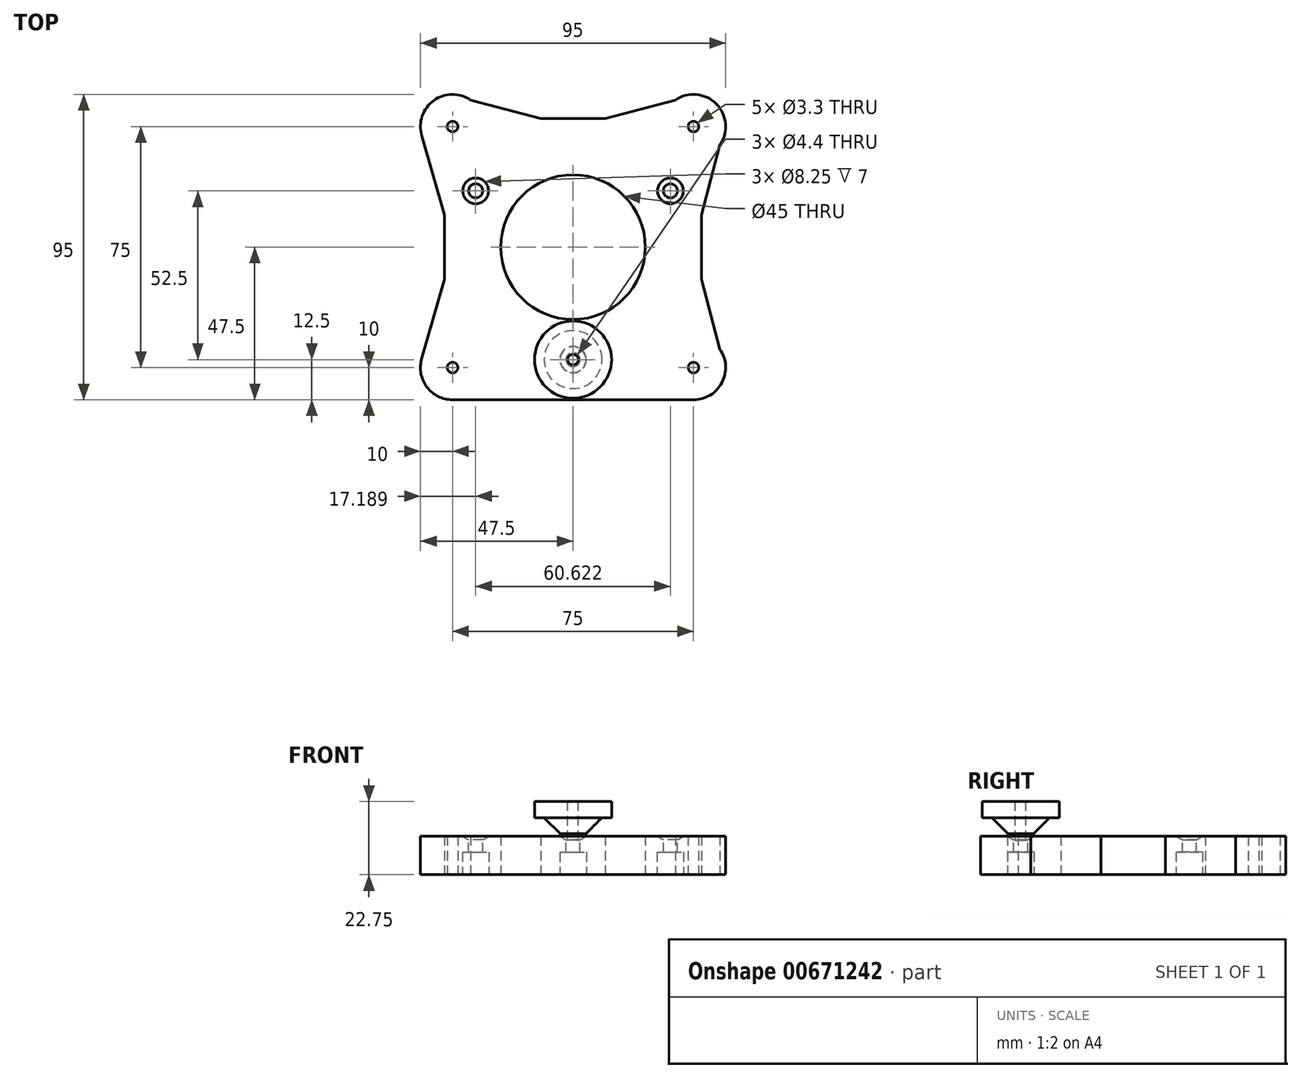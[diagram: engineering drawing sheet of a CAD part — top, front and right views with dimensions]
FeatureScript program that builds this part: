
annotation { "Feature Type Name" : "Feature", "Feature Type Description" : "" }
export const myFeature = defineFeature(function(context is Context, id is Id, definition is map)
    precondition{}
    {
        {
            var Q0;
            Q0=qCreatedBy(makeId("Top.planeOp"),FACE);
            var sketch = newSketch(context, id + "F0", { "sketchPlane" : qUnion([Q0])});
            skLineSegment(sketch, "E0", {"start": v(0, -66.49) * mm, "end": v(0, 82.54) * mm, "construction": true});
            skLineSegment(sketch, "E1", {"start": v(68.94, 0) * mm, "end": v(-65.72, 0) * mm, "construction": true});
            skLineSegment(sketch, "E2.MirrorCS", {"start": v(-68.94, 0) * mm, "end": v(65.72, 0) * mm, "construction": true});
            skArc(sketch, "E3", {"start": v(-31.85, 45.75) * mm, "mid": v(-43.35, 45.6) * mm, "end": v(-47.11, 34.74) * mm});
            skArc(sketch, "E4", {"start": v(45.75, 31.85) * mm, "mid": v(44.57, 44.57) * mm, "end": v(31.85, 45.75) * mm});
            skArc(sketch, "E5", {"start": v(37.5, -47.5) * mm, "mid": v(46.35, -42.16) * mm, "end": v(45.75, -31.85) * mm});
            skArc(sketch, "E6", {"start": v(-47.11, -34.74) * mm, "mid": v(-45.49, -43.52) * mm, "end": v(-37.5, -47.5) * mm});
            skLineSegment(sketch, "E7", {"start": v(-40, -10) * mm, "end": v(-40, 10) * mm});
            skLineSegment(sketch, "E8", {"start": v(-40, 10) * mm, "end": v(-47.11, 34.74) * mm});
            skLineSegment(sketch, "E9", {"start": v(-40, -10) * mm, "end": v(-47.11, -34.74) * mm});
            skLineSegment(sketch, "E10.2.0", {"start": v(40, 10) * mm, "end": v(40, -10) * mm});
            skLineSegment(sketch, "E10.2.1", {"start": v(40, -10) * mm, "end": v(45.75, -31.85) * mm});
            skLineSegment(sketch, "E10.2.2", {"start": v(40, 10) * mm, "end": v(45.75, 31.85) * mm});
            skLineSegment(sketch, "E10.3.0", {"start": v(-10, 40) * mm, "end": v(10, 40) * mm});
            skLineSegment(sketch, "E10.3.1", {"start": v(10, 40) * mm, "end": v(31.85, 45.75) * mm});
            skLineSegment(sketch, "E10.3.2", {"start": v(-10, 40) * mm, "end": v(-31.85, 45.75) * mm});
            skPoint(sketch, "E10.center", {"position": v(0, 0) * mm});
            skLineSegment(sketch, "E11", {"start": v(-37.5, -47.5) * mm, "end": v(37.5, -47.5) * mm});
            skSolve(sketch);
        }
        {
            var Q0;
            Q0=makeQuery(id+"F0.imprint","IMPRINT",FACE,{"disambiguationData":[TD([[makeQuery(id+"F0.imprint","IMPRINT",EDGE,{"derivedFrom":sQuery(id+"F0.wireOp",EDGE,"E3")}),1.0]])]});
            extrude(context, id + "F1", {"entities" : qUnion([Q0]), "depth" : 12 * mm, "offsetDistance" : 25 * mm});
        }
        {
            var Q0;
            Q0=makeQuery(id+"F1.opExtrude","CAP_FACE",FACE,{"disambiguationData":[OSD([sQuery(id+"F0.wireOp",EDGE,"H59K7WDl-hRpV-Jpdm-ny2t-aA3Kgsrr1DyG"),sQuery(id+"F0.wireOp",EDGE,"7fe8aba1-2dff-4e51-9fbd-37248f7f35f50.MirrorC"),sQuery(id+"F0.wireOp",EDGE,"c00ab9d0-4618-4e23-ab7e-bcd3a19236070.MirrorC"),sQuery(id+"F0.wireOp",EDGE,"2b578c46-e155-4f13-8c82-5516d9e6c2640.MirrorC"),sQuery(id+"F0.wireOp",EDGE,"E3"),sQuery(id+"F0.wireOp",EDGE,"E4"),sQuery(id+"F0.wireOp",EDGE,"E5"),sQuery(id+"F0.wireOp",EDGE,"E6"),sQuery(id+"F0.wireOp",EDGE,"E7"),sQuery(id+"F0.wireOp",EDGE,"E8"),sQuery(id+"F0.wireOp",EDGE,"E9"),sQuery(id+"F0.wireOp",EDGE,"E10.1.1"),sQuery(id+"F0.wireOp",EDGE,"E10.1.2"),sQuery(id+"F0.wireOp",EDGE,"E10.2.0"),sQuery(id+"F0.wireOp",EDGE,"E10.2.1"),sQuery(id+"F0.wireOp",EDGE,"E10.2.2"),sQuery(id+"F0.wireOp",EDGE,"E10.3.0"),sQuery(id+"F0.wireOp",EDGE,"E10.3.1"),sQuery(id+"F0.wireOp",EDGE,"E10.3.2"),sQuery(id+"F0.wireOp",EDGE,"E11")])],"isStart":false});
            var sketch = newSketch(context, id + "F2", { "sketchPlane" : qUnion([Q0])});
            skLineSegment(sketch, "E12", {"start": v(0, 0) * mm, "end": v(0, -80.34) * mm, "construction": true});
            skPoint(sketch, "E13", {"position": v(0, -35) * mm});
            skPoint(sketch, "E14.center", {"position": v(0, 0) * mm});
            skPoint(sketch, "E15.1.0", {"position": v(30.31, 17.5) * mm});
            skPoint(sketch, "E15.2.0", {"position": v(-30.31, 17.5) * mm});
            skLineSegment(sketch, "E16", {"start": v(0, -20.19) * mm, "end": v(0, -35) * mm, "construction": true});
            skLineSegment(sketch, "E17.1.0", {"start": v(17.48, 10.1) * mm, "end": v(30.31, 17.5) * mm, "construction": true});
            skLineSegment(sketch, "E17.2.0", {"start": v(-17.48, 10.1) * mm, "end": v(-30.31, 17.5) * mm, "construction": true});
            skSolve(sketch);
        }
        {
            var Q0;
            Q0=sQuery(id+"F2.wireOp",VERTEX,"E13");
            var Q1;
            Q1=makeQuery(id+"F1.opExtrude","SWEPT_FACE",FACE,{"disambiguationData":[OSD([sQuery(id+"F0.wireOp",EDGE,"E10.3.0")])]});
            cPlane(context, id + "F3", {"entities" : qUnion([Q0, Q1]), "cplaneType" : CPlaneType.PLANE_POINT, "offset" : 25 * mm, "width" : 150 * mm, "height" : 150 * mm});
        }
        {
            var Q0;
            Q0=qCreatedBy(id+"F3.planeOp",FACE);
            var sketch = newSketch(context, id + "F4", { "sketchPlane" : qUnion([Q0])});
            skLineSegment(sketch, "E18", {"start": v(4, 12) * mm, "end": v(0, 12) * mm});
            skArc(sketch, "E19", {"start": v(0, 10.47) * mm, "mid": v(2.14, 10.87) * mm, "end": v(4, 12) * mm});
            skLineSegment(sketch, "E20", {"start": v(0, 12) * mm, "end": v(0, 40.48) * mm, "construction": true});
            skLineSegment(sketch, "E21", {"start": v(0, 12) * mm, "end": v(0, 10.47) * mm});
            skLineSegment(sketch, "E22.trimOffspring", {"start": v(0, 12) * mm, "end": v(4, 12) * mm});
            skPoint(sketch, "E23.0.8.end.orphan", {"position": v(-4, 12) * mm});
            skPoint(sketch, "E23.0.8.start.orphan", {"position": v(-10, 12) * mm});
            skPoint(sketch, "E24.orphan", {"position": v(10, 12) * mm});
            skSolve(sketch);
        }
        {
            var Q0;
            Q0=sQuery(id+"F2.wireOp",EDGE,"E17.2.0");
            cPlane(context, id + "F5", {"entities" : qUnion([Q0]), "cplaneType" : CPlaneType.LINE_ANGLE, "offset" : 25 * mm, "angle" : 0 * degree, "width" : 150 * mm, "height" : 150 * mm});
        }
        {
            var Q0;
            Q0=qCreatedBy(id+"F5.planeOp",FACE);
            var sketch = newSketch(context, id + "F6", { "sketchPlane" : qUnion([Q0])});
            skLineSegment(sketch, "E25", {"start": v(-31, 12) * mm, "end": v(-35, 12) * mm});
            skArc(sketch, "E26", {"start": v(-35, 10.47) * mm, "mid": v(-32.86, 10.87) * mm, "end": v(-31, 12) * mm});
            skLineSegment(sketch, "E27", {"start": v(-35, 12) * mm, "end": v(-35, 40.48) * mm, "construction": true});
            skLineSegment(sketch, "E28", {"start": v(-35, 12) * mm, "end": v(-35, 10.47) * mm});
            skLineSegment(sketch, "E29.trimOffspring", {"start": v(-35, 12) * mm, "end": v(-31, 12) * mm});
            skPoint(sketch, "E30.0.8.end.orphan", {"position": v(-39, 12) * mm});
            skPoint(sketch, "E30.0.8.start.orphan", {"position": v(-45, 12) * mm});
            skPoint(sketch, "E31.orphan", {"position": v(-25, 12) * mm});
            skSolve(sketch);
        }
        {
            var Q0;
            {var subQ0=sQuery(id+"F4.wireOp",EDGE,"E19");Q0=makeQuery(id+"F4.imprint","IMPRINT",FACE,{"disambiguationData":[TD([[makeQuery(id+"F4.imprint","IMPRINT",EDGE,{"derivedFrom":subQ0}),1.0]])]});}
            var Q1;
            Q1=sQuery(id+"F4.wireOp",EDGE,"E20");
            revolve(context, id + "F7", {"operationType" : NewBodyOperationType.REMOVE, "entities" : qUnion([Q0]), "axis" : qUnion([Q1]), "revolveType" : RevolveType.FULL, "oppositeDirection" : true});
        }
        {
            var Q0;
            Q0=makeQuery(id+"F6.imprint","IMPRINT",FACE,{"disambiguationData":[TD([[makeQuery(id+"F6.imprint","IMPRINT",EDGE,{"derivedFrom":sQuery(id+"F6.wireOp",EDGE,"E26")}),1.0]])]});
            var Q1;
            Q1=sQuery(id+"F6.wireOp",EDGE,"E27");
            revolve(context, id + "F8", {"operationType" : NewBodyOperationType.REMOVE, "entities" : qUnion([Q0]), "axis" : qUnion([Q1]), "revolveType" : RevolveType.FULL, "oppositeDirection" : true});
        }
        {
            var Q0;
            Q0=sQuery(id+"F2.wireOp",EDGE,"E17.1.0");
            cPlane(context, id + "F9", {"entities" : qUnion([Q0]), "cplaneType" : CPlaneType.LINE_ANGLE, "offset" : 25 * mm, "angle" : 0 * degree, "width" : 150 * mm, "height" : 150 * mm});
        }
        {
            var Q0;
            Q0=qCreatedBy(id+"F9.planeOp",FACE);
            var sketch = newSketch(context, id + "F10", { "sketchPlane" : qUnion([Q0])});
            skLineSegment(sketch, "E32", {"start": v(-31, 12) * mm, "end": v(-35, 12) * mm});
            skArc(sketch, "E33", {"start": v(-35, 10.47) * mm, "mid": v(-32.86, 10.87) * mm, "end": v(-31, 12) * mm});
            skLineSegment(sketch, "E34", {"start": v(-35, 12) * mm, "end": v(-35, 40.48) * mm, "construction": true});
            skLineSegment(sketch, "E35", {"start": v(-35, 12) * mm, "end": v(-35, 10.47) * mm});
            skLineSegment(sketch, "E36.trimOffspring", {"start": v(-35, 12) * mm, "end": v(-31, 12) * mm});
            skPoint(sketch, "E37.0.8.end.orphan", {"position": v(-39, 12) * mm});
            skPoint(sketch, "E37.0.8.start.orphan", {"position": v(-45, 12) * mm});
            skPoint(sketch, "E38.orphan", {"position": v(-25, 12) * mm});
            skSolve(sketch);
        }
        {
            var Q0;
            Q0=makeQuery(id+"F10.imprint","IMPRINT",FACE,{"disambiguationData":[TD([[makeQuery(id+"F10.imprint","IMPRINT",EDGE,{"derivedFrom":sQuery(id+"F10.wireOp",EDGE,"E33")}),1.0]])]});
            var Q1;
            Q1=sQuery(id+"F10.wireOp",EDGE,"E34");
            revolve(context, id + "F11", {"operationType" : NewBodyOperationType.REMOVE, "entities" : qUnion([Q0]), "axis" : qUnion([Q1]), "revolveType" : RevolveType.FULL, "oppositeDirection" : true});
        }
        {
            var Q0;
            Q0=qCreatedBy(id+"F3.planeOp",FACE);
            var sketch = newSketch(context, id + "F12", { "sketchPlane" : qUnion([Q0])});
            skPoint(sketch, "E39.0", {"position": v(0, 12) * mm});
            skArc(sketch, "E40", {"start": v(0, 10.47) * mm, "mid": v(2.14, 10.87) * mm, "end": v(4, 12) * mm});
            skLineSegment(sketch, "E41", {"start": v(0, 12) * mm, "end": v(0, 10.47) * mm});
            skPoint(sketch, "E42.orphan", {"position": v(-4, 12) * mm});
            skLineSegment(sketch, "E43", {"start": v(4, 12) * mm, "end": v(4, 17.75) * mm});
            skLineSegment(sketch, "E44", {"start": v(4, 17.75) * mm, "end": v(12, 17.75) * mm});
            skLineSegment(sketch, "E45", {"start": v(12, 17.75) * mm, "end": v(12, 22.75) * mm});
            skLineSegment(sketch, "E46", {"start": v(12, 22.75) * mm, "end": v(0, 22.75) * mm});
            skLineSegment(sketch, "E47", {"start": v(0, 22.75) * mm, "end": v(0, 16.47) * mm});
            skLineSegment(sketch, "E48", {"start": v(0, 16.47) * mm, "end": v(0, 12) * mm});
            skSolve(sketch);
        }
        {
            var Q0;
            Q0 = qSketchRegion(id + "F12", true);
            var Q1;
            Q1=sQuery(id+"F12.wireOp",EDGE,"E47");
            revolve(context, id + "F13", {"entities" : qUnion([Q0]), "axis" : qUnion([Q1]), "revolveType" : RevolveType.FULL});
        }
        {
            var Q0;
            Q0=makeQuery(id+"F13.opRevolve","SWEPT_FACE",FACE,{"disambiguationData":[OSD([sQuery(id+"F12.wireOp",EDGE,"E46")])]});
            var sketch = newSketch(context, id + "F14", { "sketchPlane" : qUnion([Q0])});
            skPoint(sketch, "E49", {"position": v(0, -35) * mm});
            skSolve(sketch);
        }
        {
            var Q0;
            Q0=sQuery(id+"F14.wireOp",VERTEX,"E49");
            var Q1;
            Q1=makeQuery(id+"F13.opRevolve","SWEPT_BODY",BODY,{"disambiguationData":[OSD([sQuery(id+"F12.wireOp",EDGE,"E40"),sQuery(id+"F12.wireOp",EDGE,"E41"),sQuery(id+"F12.wireOp",EDGE,"E43"),sQuery(id+"F12.wireOp",EDGE,"E44"),sQuery(id+"F12.wireOp",EDGE,"E45"),sQuery(id+"F12.wireOp",EDGE,"E46"),sQuery(id+"F12.wireOp",EDGE,"E47"),sQuery(id+"F12.wireOp",EDGE,"E48")])]});
            hole(context, id + "F15", {"style" : HoleStyle.SIMPLE, "endStyle" : HoleEndStyle.THROUGH, "standardTappedOrClearance" : lookupTablePath({ "standard" : "ISO", "engagement" : "75%", "pitch" : "0.7 mm", "size" : "M4", "type" : "Tapped" }), "standardBlindInLast" : lookupTablePath({ "standard" : "ISO", "engagement" : "75%", "pitch" : "0.7 mm", "size" : "M4", "type" : "Tapped" }), "holeDiameter" : 3.3 * mm, "majorDiameter" : 4 * mm, "showTappedDepth" : true, "isTappedThrough" : true, "tappedDepth" : 12 * mm, "tapClearance" : 3, "locations" : qUnion([Q0]), "scope" : qUnion([Q1])});
        }
        {
            var Q0;
            Q0=sQuery(id+"F2.wireOp",VERTEX,"E15.1.0");
            var Q1;
            Q1=sQuery(id+"F2.wireOp",VERTEX,"E15.2.0");
            var Q2;
            Q2=sQuery(id+"F2.wireOp",VERTEX,"E13");
            var Q3;
            Q3=makeQuery(id+"F1.opExtrude","SWEPT_BODY",BODY,{"disambiguationData":[OSD([sQuery(id+"F0.wireOp",EDGE,"H59K7WDl-hRpV-Jpdm-ny2t-aA3Kgsrr1DyG"),sQuery(id+"F0.wireOp",EDGE,"7fe8aba1-2dff-4e51-9fbd-37248f7f35f50.MirrorC"),sQuery(id+"F0.wireOp",EDGE,"c00ab9d0-4618-4e23-ab7e-bcd3a19236070.MirrorC"),sQuery(id+"F0.wireOp",EDGE,"2b578c46-e155-4f13-8c82-5516d9e6c2640.MirrorC"),sQuery(id+"F0.wireOp",EDGE,"E3"),sQuery(id+"F0.wireOp",EDGE,"E4"),sQuery(id+"F0.wireOp",EDGE,"E5"),sQuery(id+"F0.wireOp",EDGE,"E6"),sQuery(id+"F0.wireOp",EDGE,"E7"),sQuery(id+"F0.wireOp",EDGE,"E8"),sQuery(id+"F0.wireOp",EDGE,"E9"),sQuery(id+"F0.wireOp",EDGE,"E10.1.1"),sQuery(id+"F0.wireOp",EDGE,"E10.1.2"),sQuery(id+"F0.wireOp",EDGE,"E10.2.0"),sQuery(id+"F0.wireOp",EDGE,"E10.2.1"),sQuery(id+"F0.wireOp",EDGE,"E10.2.2"),sQuery(id+"F0.wireOp",EDGE,"E10.3.0"),sQuery(id+"F0.wireOp",EDGE,"E10.3.1"),sQuery(id+"F0.wireOp",EDGE,"E10.3.2"),sQuery(id+"F0.wireOp",EDGE,"E11")])]});
            hole(context, id + "F16", {"style" : HoleStyle.SIMPLE, "endStyle" : HoleEndStyle.THROUGH, "standardTappedOrClearance" : lookupTablePath({ "standard" : "ISO", "fit" : "Normal", "size" : "M4", "type" : "Clearance" }), "standardBlindInLast" : lookupTablePath({ "fit" : "Standard", "standard" : "ISO", "size" : "M4", "type" : "Clearance" }), "holeDiameter" : 4.4 * mm, "majorDiameter" : 4 * mm, "isTappedThrough" : true, "tappedDepth" : 12 * mm, "tapClearance" : 3, "locations" : qUnion([Q0, Q1, Q2]), "scope" : qUnion([Q3])});
        }
        {
            var Q0;
            Q0=makeQuery(id+"F1.opExtrude","CAP_FACE",FACE,{"disambiguationData":[OSD([sQuery(id+"F0.wireOp",EDGE,"H59K7WDl-hRpV-Jpdm-ny2t-aA3Kgsrr1DyG"),sQuery(id+"F0.wireOp",EDGE,"7fe8aba1-2dff-4e51-9fbd-37248f7f35f50.MirrorC"),sQuery(id+"F0.wireOp",EDGE,"c00ab9d0-4618-4e23-ab7e-bcd3a19236070.MirrorC"),sQuery(id+"F0.wireOp",EDGE,"2b578c46-e155-4f13-8c82-5516d9e6c2640.MirrorC"),sQuery(id+"F0.wireOp",EDGE,"E3"),sQuery(id+"F0.wireOp",EDGE,"E4"),sQuery(id+"F0.wireOp",EDGE,"E5"),sQuery(id+"F0.wireOp",EDGE,"E6"),sQuery(id+"F0.wireOp",EDGE,"E7"),sQuery(id+"F0.wireOp",EDGE,"E8"),sQuery(id+"F0.wireOp",EDGE,"E9"),sQuery(id+"F0.wireOp",EDGE,"E10.1.1"),sQuery(id+"F0.wireOp",EDGE,"E10.1.2"),sQuery(id+"F0.wireOp",EDGE,"E10.2.0"),sQuery(id+"F0.wireOp",EDGE,"E10.2.1"),sQuery(id+"F0.wireOp",EDGE,"E10.2.2"),sQuery(id+"F0.wireOp",EDGE,"E10.3.0"),sQuery(id+"F0.wireOp",EDGE,"E10.3.1"),sQuery(id+"F0.wireOp",EDGE,"E10.3.2"),sQuery(id+"F0.wireOp",EDGE,"E11")])],"isStart":true});
            var sketch = newSketch(context, id + "F17", { "sketchPlane" : qUnion([Q0])});
            skPoint(sketch, "E50", {"position": v(-30.31, -17.5) * mm});
            skPoint(sketch, "E51", {"position": v(0, 35) * mm});
            skPoint(sketch, "E52", {"position": v(30.31, -17.5) * mm});
            skSolve(sketch);
        }
        {
            var Q0;
            Q0=sQuery(id+"F17.wireOp",VERTEX,"E50");
            var Q1;
            Q1=sQuery(id+"F17.wireOp",VERTEX,"E51");
            var Q2;
            Q2=sQuery(id+"F17.wireOp",VERTEX,"E52");
            var Q3;
            Q3=makeQuery(id+"F1.opExtrude","SWEPT_BODY",BODY,{"disambiguationData":[OSD([sQuery(id+"F0.wireOp",EDGE,"H59K7WDl-hRpV-Jpdm-ny2t-aA3Kgsrr1DyG"),sQuery(id+"F0.wireOp",EDGE,"7fe8aba1-2dff-4e51-9fbd-37248f7f35f50.MirrorC"),sQuery(id+"F0.wireOp",EDGE,"c00ab9d0-4618-4e23-ab7e-bcd3a19236070.MirrorC"),sQuery(id+"F0.wireOp",EDGE,"2b578c46-e155-4f13-8c82-5516d9e6c2640.MirrorC"),sQuery(id+"F0.wireOp",EDGE,"E3"),sQuery(id+"F0.wireOp",EDGE,"E4"),sQuery(id+"F0.wireOp",EDGE,"E5"),sQuery(id+"F0.wireOp",EDGE,"E6"),sQuery(id+"F0.wireOp",EDGE,"E7"),sQuery(id+"F0.wireOp",EDGE,"E8"),sQuery(id+"F0.wireOp",EDGE,"E9"),sQuery(id+"F0.wireOp",EDGE,"E10.1.1"),sQuery(id+"F0.wireOp",EDGE,"E10.1.2"),sQuery(id+"F0.wireOp",EDGE,"E10.2.0"),sQuery(id+"F0.wireOp",EDGE,"E10.2.1"),sQuery(id+"F0.wireOp",EDGE,"E10.2.2"),sQuery(id+"F0.wireOp",EDGE,"E10.3.0"),sQuery(id+"F0.wireOp",EDGE,"E10.3.1"),sQuery(id+"F0.wireOp",EDGE,"E10.3.2"),sQuery(id+"F0.wireOp",EDGE,"E11")])]});
            hole(context, id + "F18", {"style" : HoleStyle.C_BORE, "endStyle" : HoleEndStyle.BLIND, "holeDiameter" : 4.4 * mm, "cBoreDiameter" : 8.25 * mm, "cBoreDepth" : 7 * mm, "majorDiameter" : 5 * mm, "holeDepth" : 7.1 * mm, "isTappedThrough" : true, "tappedDepth" : 12 * mm, "tapClearance" : 3, "locations" : qUnion([Q0, Q1, Q2]), "scope" : qUnion([Q3])});
        }
        {
            var Q0;
            Q0=sQuery(id+"F0.wireOp",VERTEX,"E3.center");
            var Q1;
            Q1=sQuery(id+"F0.wireOp",VERTEX,"E6.center");
            var Q2;
            Q2=sQuery(id+"F0.wireOp",VERTEX,"E5.center");
            var Q3;
            Q3=sQuery(id+"F0.wireOp",VERTEX,"E4.center");
            var Q4;
            Q4=makeQuery(id+"F1.opExtrude","SWEPT_BODY",BODY,{"disambiguationData":[OSD([sQuery(id+"F0.wireOp",EDGE,"E3"),sQuery(id+"F0.wireOp",EDGE,"E4"),sQuery(id+"F0.wireOp",EDGE,"E5"),sQuery(id+"F0.wireOp",EDGE,"E6"),sQuery(id+"F0.wireOp",EDGE,"E7"),sQuery(id+"F0.wireOp",EDGE,"E8"),sQuery(id+"F0.wireOp",EDGE,"E9"),sQuery(id+"F0.wireOp",EDGE,"E10.1.1"),sQuery(id+"F0.wireOp",EDGE,"E10.1.2"),sQuery(id+"F0.wireOp",EDGE,"E10.2.0"),sQuery(id+"F0.wireOp",EDGE,"E10.2.1"),sQuery(id+"F0.wireOp",EDGE,"E10.2.2"),sQuery(id+"F0.wireOp",EDGE,"E10.3.0"),sQuery(id+"F0.wireOp",EDGE,"E10.3.1"),sQuery(id+"F0.wireOp",EDGE,"E10.3.2"),sQuery(id+"F0.wireOp",EDGE,"E11")])]});
            hole(context, id + "F19", {"style" : HoleStyle.SIMPLE, "endStyle" : HoleEndStyle.THROUGH, "oppositeDirection" : true, "standardTappedOrClearance" : lookupTablePath({ "standard" : "ISO", "engagement" : "75%", "pitch" : "0.7 mm", "size" : "M4", "type" : "Tapped" }), "standardBlindInLast" : lookupTablePath({ "standard" : "ISO", "engagement" : "75%", "pitch" : "0.7 mm", "size" : "M4", "type" : "Tapped" }), "holeDiameter" : 3.3 * mm, "majorDiameter" : 4 * mm, "showTappedDepth" : true, "isTappedThrough" : true, "tappedDepth" : 12 * mm, "tapClearance" : 3, "locations" : qUnion([Q0, Q1, Q2, Q3]), "scope" : qUnion([Q4])});
        }
        {
            var Q0;
            Q0=makeQuery(id+"F0.imprint","IMPRINT",FACE,{"disambiguationData":[TD([[makeQuery(id+"F0.imprint","IMPRINT",EDGE,{"derivedFrom":sQuery(id+"F0.wireOp",EDGE,"E3")}),1.0]])]});
            var sketch = newSketch(context, id + "F20", { "sketchPlane" : qUnion([Q0])});
            skCircle(sketch, "E53", {"center": v(0, 0) * mm, "radius": 22.5 * mm});
            skSolve(sketch);
        }
        {
            var Q0;
            Q0=makeQuery(id+"F20.imprint","IMPRINT",FACE,{"disambiguationData":[TD([[makeQuery(id+"F20.imprint","IMPRINT",EDGE,{"derivedFrom":sQuery(id+"F20.wireOp",EDGE,"E53")}),1.0]])]});
            extrude(context, id + "F21", {"entities" : qUnion([Q0]), "operationType" : NewBodyOperationType.REMOVE, "endBound" : BoundingType.UP_TO_NEXT, "depth" : 25 * mm, "offsetDistance" : 25 * mm});
        }
        {
            var Q0;
            Q0=makeQuery(id+"F13.opRevolve","SWEPT_EDGE",EDGE,{"disambiguationData":[OSD([sQuery(id+"F12.wireOp",EDGE,"E43"),sQuery(id+"F12.wireOp",EDGE,"E44")])]});
            chamfer(context, id + "F22", {"entities" : qUnion([Q0]), "width" : 5 * mm, "tangentPropagation" : true});
        }
    });
